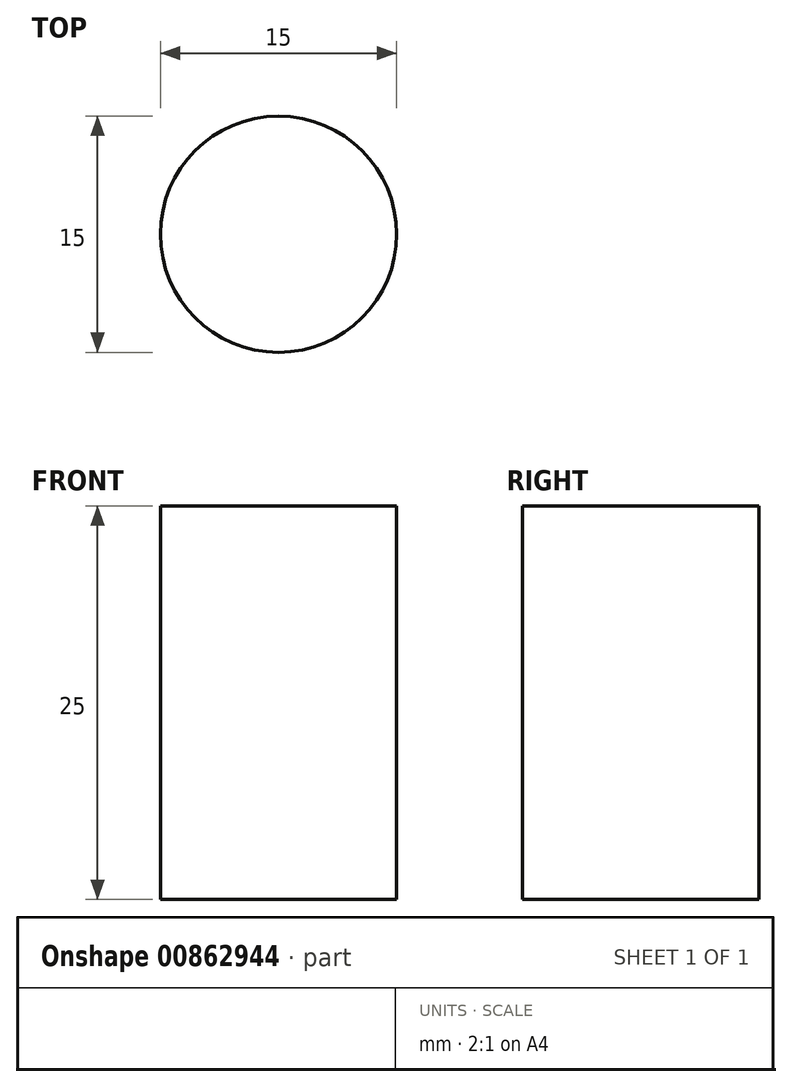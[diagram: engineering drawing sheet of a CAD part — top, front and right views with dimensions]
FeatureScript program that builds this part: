
annotation { "Feature Type Name" : "Feature", "Feature Type Description" : "" }
export const myFeature = defineFeature(function(context is Context, id is Id, definition is map)
    precondition{}
    {
        {
            var Q0;
            Q0=qCreatedBy(makeId("Top.planeOp"),FACE);
            var sketch = newSketch(context, id + "F0", { "sketchPlane" : qUnion([Q0])});
            skCircle(sketch, "E0", {"center": v(0, 0) * mm, "radius": 7.5 * mm});
            skSolve(sketch);
        }
        {
            var Q0;
            Q0 = qSketchRegion(id + "F0", true);
            extrude(context, id + "F1", {"entities" : qUnion([Q0]), "depth" : 25 * mm, "offsetDistance" : 25 * mm});
        }
    });
